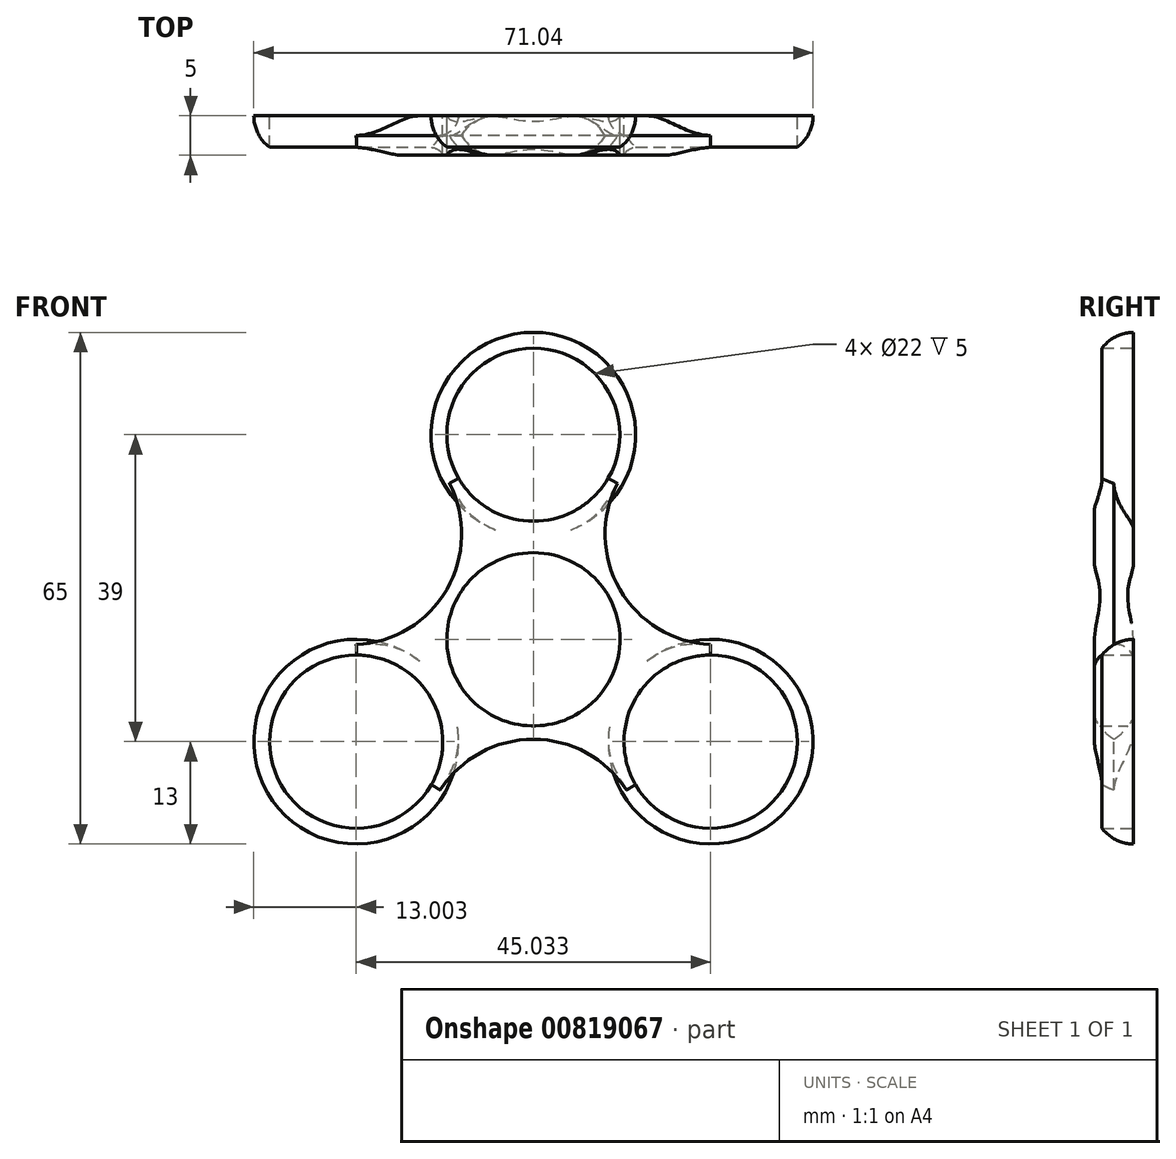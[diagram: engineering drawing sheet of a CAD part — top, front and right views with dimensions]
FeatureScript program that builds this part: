
annotation { "Feature Type Name" : "Feature", "Feature Type Description" : "" }
export const myFeature = defineFeature(function(context is Context, id is Id, definition is map)
    precondition{}
    {
        {
            var Q0;
            Q0=qCreatedBy(makeId("Front.planeOp"),FACE);
            var sketch = newSketch(context, id + "F0", { "sketchPlane" : qUnion([Q0])});
            skCircle(sketch, "E0", {"center": v(0, 0) * mm, "radius": 11 * mm});
            skCircle(sketch, "E1.0", {"center": v(0, 0) * mm, "radius": 13 * mm});
            skCircle(sketch, "E2", {"center": v(0, 26) * mm, "radius": 11 * mm});
            skCircle(sketch, "E3.0", {"center": v(0, 26) * mm, "radius": 13 * mm});
            skCircle(sketch, "E4.1.0", {"center": v(-22.52, -13) * mm, "radius": 11 * mm});
            skCircle(sketch, "E4.1.1", {"center": v(-22.52, -13) * mm, "radius": 13 * mm});
            skCircle(sketch, "E4.2.0", {"center": v(22.52, -13) * mm, "radius": 11 * mm});
            skCircle(sketch, "E4.2.1", {"center": v(22.52, -13) * mm, "radius": 13 * mm});
            skArc(sketch, "E5", {"start": v(11.26, 19.5) * mm, "mid": v(11.57, 6.68) * mm, "end": v(22.52, 0) * mm});
            skArc(sketch, "E6.1.0", {"start": v(-22.52, 0) * mm, "mid": v(-11.57, 6.68) * mm, "end": v(-11.26, 19.5) * mm});
            skArc(sketch, "E6.2.0", {"start": v(11.26, -19.5) * mm, "mid": v(0, -13.37) * mm, "end": v(-11.26, -19.5) * mm});
            skSolve(sketch);
        }
        {
            var Q0;
            Q0 = qSketchRegion(id + "F0", true);
            var Q1;
            Q1=makeQuery(id+"F0.imprint","IMPRINT",FACE,{"disambiguationData":[TD([[makeQuery(id+"F0.imprint","IMPRINT",EDGE,{"derivedFrom":sQuery(id+"F0.wireOp",EDGE,"E0")}),-1.0]])]});
            extrude(context, id + "F1", {"entities" : qUnion([Q0, Q1]), "depth" : 5 * mm, "offsetDistance" : 25 * mm});
        }
        {
            var Q0;
            Q0=makeQuery(id+"F1.opExtrude","CAP_EDGE",EDGE,{"disambiguationData":[OSD([sQuery(id+"F0.wireOp",EDGE,"E6.2.0")])],"isStart":false});
            var Q1;
            Q1=makeQuery(id+"F1.opExtrude","CAP_EDGE",EDGE,{"disambiguationData":[OSD([sQuery(id+"F0.wireOp",EDGE,"E6.2.0")])],"isStart":true});
            var Q2;
            Q2=makeQuery(id+"F1.opExtrude","CAP_EDGE",EDGE,{"disambiguationData":[OSD([sQuery(id+"F0.wireOp",EDGE,"E5")])],"isStart":true});
            var Q3;
            Q3=makeQuery(id+"F1.opExtrude","CAP_EDGE",EDGE,{"disambiguationData":[OSD([sQuery(id+"F0.wireOp",EDGE,"E5")])],"isStart":false});
            var Q4;
            Q4=makeQuery(id+"F1.opExtrude","CAP_EDGE",EDGE,{"disambiguationData":[OSD([sQuery(id+"F0.wireOp",EDGE,"E6.1.0")])],"isStart":false});
            var Q5;
            Q5=makeQuery(id+"F1.opExtrude","CAP_EDGE",EDGE,{"disambiguationData":[OSD([sQuery(id+"F0.wireOp",EDGE,"E6.1.0")])],"isStart":true});
            fillet(context, id + "F2", {"entities" : qUnion([Q0, Q1, Q2, Q3, Q4, Q5]), "radius" : 5 * mm, "tangentPropagation" : true, "allowEdgeOverflow" : false});
        }
        {
            var Q0;
            Q0=makeQuery(id+"F1.opExtrude","CAP_EDGE",EDGE,{"disambiguationData":[OSD([sQuery(id+"F0.wireOp",EDGE,"E3.0")])],"isStart":false});
            var Q1;
            Q1=makeQuery(id+"F1.opExtrude","CAP_EDGE",EDGE,{"disambiguationData":[OSD([sQuery(id+"F0.wireOp",EDGE,"E4.2.1")])],"isStart":false});
            var Q2;
            Q2=makeQuery(id+"F1.opExtrude","CAP_EDGE",EDGE,{"disambiguationData":[OSD([sQuery(id+"F0.wireOp",EDGE,"E4.1.1")])],"isStart":false});
            fillet(context, id + "F3", {"entities" : qUnion([Q0, Q1, Q2]), "radius" : 5 * mm, "tangentPropagation" : true, "allowEdgeOverflow" : false});
        }
    });
